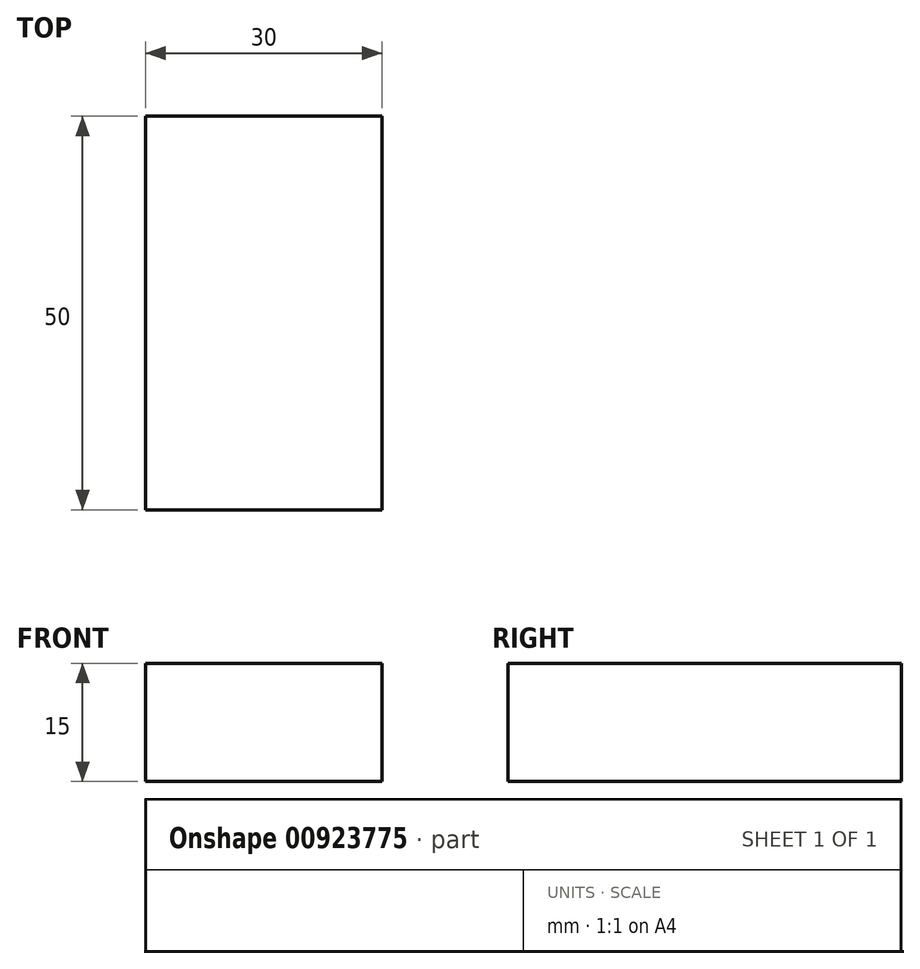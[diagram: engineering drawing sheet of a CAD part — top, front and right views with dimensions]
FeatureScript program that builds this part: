
annotation { "Feature Type Name" : "Feature", "Feature Type Description" : "" }
export const myFeature = defineFeature(function(context is Context, id is Id, definition is map)
    precondition{}
    {
        {
            var Q0;
            Q0=qCreatedBy(makeId("Top.planeOp"),FACE);
            var sketch = newSketch(context, id + "F0", { "sketchPlane" : qUnion([Q0])});
            skLineSegment(sketch, "E0", {"start": v(-90.44, 24.56) * mm, "end": v(-90.44, -25.44) * mm});
            skLineSegment(sketch, "E1", {"start": v(-90.44, -25.44) * mm, "end": v(-60.44, -25.44) * mm});
            skLineSegment(sketch, "E2", {"start": v(-60.44, -25.44) * mm, "end": v(-60.44, 24.56) * mm});
            skLineSegment(sketch, "E3", {"start": v(-60.44, 24.56) * mm, "end": v(-90.44, 24.56) * mm});
            skSolve(sketch);
        }
        {
            var Q0;
            Q0=makeQuery(id+"F0.imprint","IMPRINT",FACE,{"disambiguationData":[TD([[makeQuery(id+"F0.imprint","IMPRINT",EDGE,{"derivedFrom":sQuery(id+"F0.wireOp",EDGE,"E0")}),1.0]])]});
            extrude(context, id + "F1", {"entities" : qUnion([Q0]), "depth" : 15 * mm, "offsetDistance" : 25 * mm});
        }
    });
